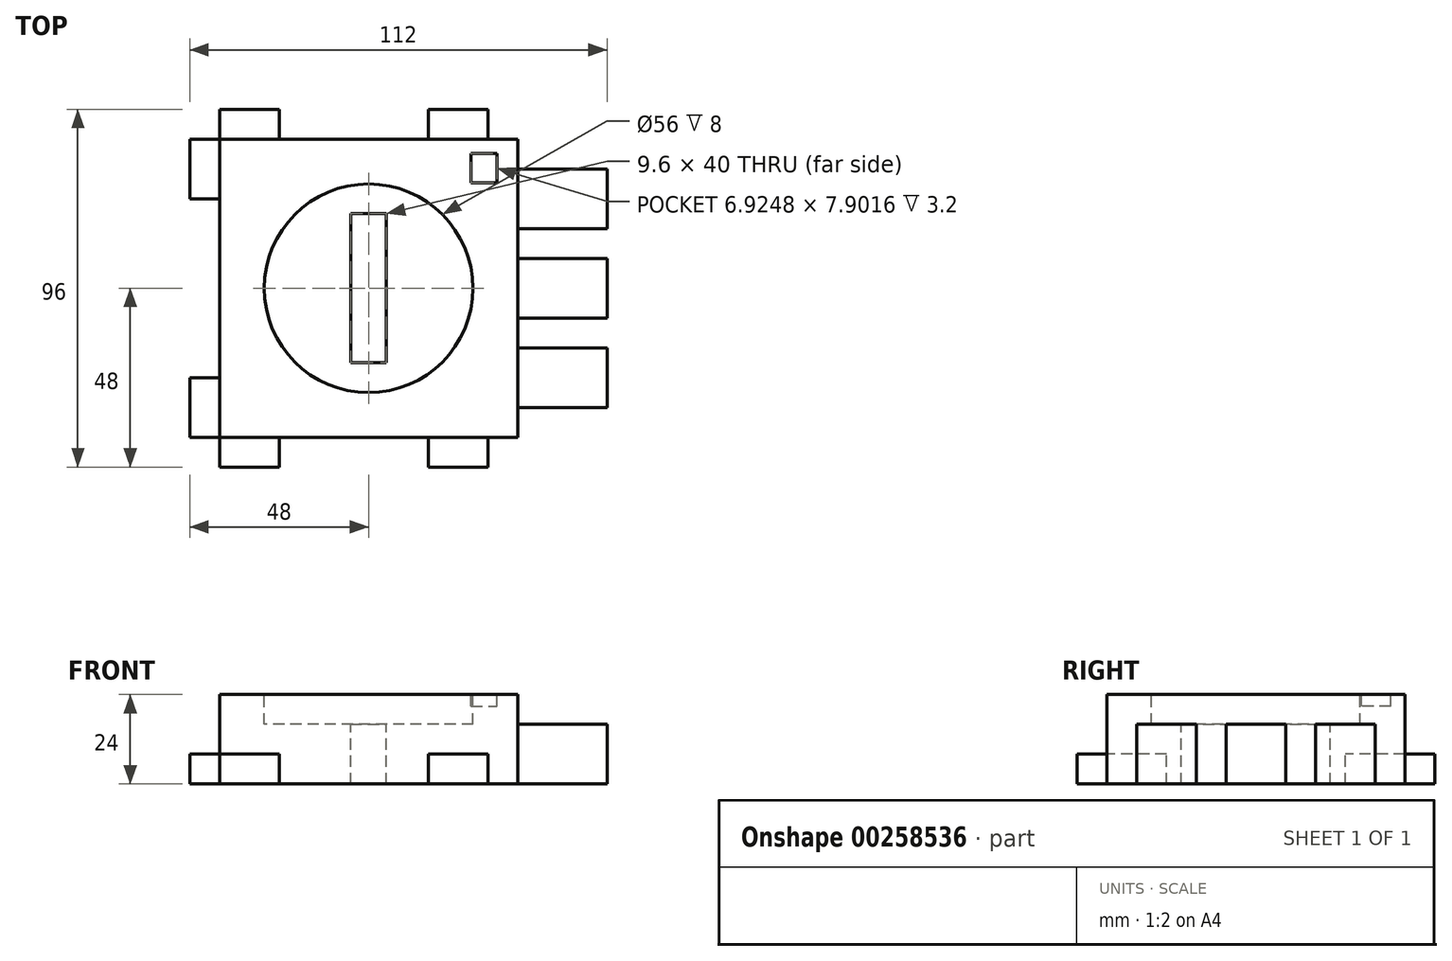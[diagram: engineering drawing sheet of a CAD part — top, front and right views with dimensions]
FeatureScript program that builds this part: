
annotation { "Feature Type Name" : "Feature", "Feature Type Description" : "" }
export const myFeature = defineFeature(function(context is Context, id is Id, definition is map)
    precondition{}
    {
        {
            var Q0;
            Q0=qCreatedBy(makeId("Top.planeOp"),FACE);
            var sketch = newSketch(context, id + "F0", { "sketchPlane" : qUnion([Q0])});
            skLineSegment(sketch, "E0.bottom", {"start": v(-25, 25) * mm, "end": v(25, 25) * mm});
            skLineSegment(sketch, "E0.top", {"start": v(-25, -25) * mm, "end": v(25, -25) * mm});
            skLineSegment(sketch, "E0.left", {"start": v(-25, 25) * mm, "end": v(-25, -25) * mm});
            skLineSegment(sketch, "E0.right", {"start": v(25, 25) * mm, "end": v(25, -25) * mm});
            skPoint(sketch, "E0.middle", {"position": v(0, 0) * mm});
            skLineSegment(sketch, "E1.0", {"start": v(-30, 30) * mm, "end": v(25, 30) * mm});
            skLineSegment(sketch, "E1.1", {"start": v(-30, 30) * mm, "end": v(-30, -30) * mm});
            skLineSegment(sketch, "E1.2", {"start": v(-30, -30) * mm, "end": v(25, -30) * mm});
            skLineSegment(sketch, "E2", {"start": v(25, 30) * mm, "end": v(25, 25) * mm});
            skLineSegment(sketch, "E3", {"start": v(25, -25) * mm, "end": v(25, -30) * mm});
            skSolve(sketch);
        }
        {
            var Q0;
            Q0=makeQuery(id+"F0.imprint","IMPRINT",FACE,{"disambiguationData":[TD([[makeQuery(id+"F0.imprint","IMPRINT",EDGE,{"derivedFrom":sQuery(id+"F0.wireOp",EDGE,"E0.bottom")}),-1.0]])]});
            extrude(context, id + "F1", {"entities" : qUnion([Q0]), "depth" : 15 * mm});
        }
        {
            var Q0;
            Q0=makeQuery(id+"F1.opExtrude","CAP_FACE",FACE,{"disambiguationData":[OSD([sQuery(id+"F0.wireOp",EDGE,"E0.bottom"),sQuery(id+"F0.wireOp",EDGE,"E0.top"),sQuery(id+"F0.wireOp",EDGE,"E0.left"),sQuery(id+"F0.wireOp",EDGE,"E0.right")])],"isStart":false});
            var sketch = newSketch(context, id + "F2", { "sketchPlane" : qUnion([Q0])});
            skLineSegment(sketch, "E4.bottom", {"start": v(-3, 12.5) * mm, "end": v(3, 12.5) * mm});
            skLineSegment(sketch, "E4.top", {"start": v(-3, -12.5) * mm, "end": v(3, -12.5) * mm});
            skLineSegment(sketch, "E4.left", {"start": v(-3, 12.5) * mm, "end": v(-3, -12.5) * mm});
            skLineSegment(sketch, "E4.right", {"start": v(3, 12.5) * mm, "end": v(3, -12.5) * mm});
            skPoint(sketch, "E4.middle", {"position": v(0, 0) * mm});
            skSolve(sketch);
        }
        {
            var Q0;
            Q0=makeQuery(id+"F2.imprint","IMPRINT",FACE,{"disambiguationData":[TD([[makeQuery(id+"F2.imprint","IMPRINT",EDGE,{"derivedFrom":sQuery(id+"F2.wireOp",EDGE,"E4.bottom")}),-1.0]])]});
            extrude(context, id + "F3", {"entities" : qUnion([Q0]), "operationType" : NewBodyOperationType.REMOVE, "oppositeDirection" : true, "depth" : 25 * mm});
        }
        {
            var Q0;
            Q0=makeQuery(id+"F1.opExtrude","SWEPT_FACE",FACE,{"disambiguationData":[OSD([sQuery(id+"F0.wireOp",EDGE,"E0.right")])]});
            var sketch = newSketch(context, id + "F4", { "sketchPlane" : qUnion([Q0])});
            skLineSegment(sketch, "E5.bottom", {"start": v(5, 12.5) * mm, "end": v(-5, 12.5) * mm});
            skLineSegment(sketch, "E5.top", {"start": v(5, 2.5) * mm, "end": v(-5, 2.5) * mm});
            skLineSegment(sketch, "E5.left", {"start": v(5, 12.5) * mm, "end": v(5, 2.5) * mm});
            skLineSegment(sketch, "E5.right", {"start": v(-5, 12.5) * mm, "end": v(-5, 2.5) * mm});
            skPoint(sketch, "E5.middle", {"position": v(0, 7.5) * mm});
            skPoint(sketch, "E5.middle.positionSnap0", {"position": v(-25, 7.5) * mm});
            skPoint(sketch, "E5.centerSnap0", {"position": v(-25, 7.5) * mm});
            skLineSegment(sketch, "E6", {"start": v(-25, 7.5) * mm, "end": v(-5, 7.5) * mm, "construction": true});
            skLineSegment(sketch, "E7", {"start": v(5, 7.5) * mm, "end": v(25, 7.5) * mm, "construction": true});
            skLineSegment(sketch, "E8.bottom", {"start": v(-10, 12.5) * mm, "end": v(-20, 12.5) * mm});
            skLineSegment(sketch, "E8.top", {"start": v(-10, 2.5) * mm, "end": v(-20, 2.5) * mm});
            skLineSegment(sketch, "E8.left", {"start": v(-10, 12.5) * mm, "end": v(-10, 2.5) * mm});
            skLineSegment(sketch, "E8.right", {"start": v(-20, 12.5) * mm, "end": v(-20, 2.5) * mm});
            skPoint(sketch, "E8.middle", {"position": v(-15, 7.5) * mm});
            skLineSegment(sketch, "E9.bottom", {"start": v(20, 12.5) * mm, "end": v(10, 12.5) * mm});
            skLineSegment(sketch, "E9.top", {"start": v(20, 2.5) * mm, "end": v(10, 2.5) * mm});
            skLineSegment(sketch, "E9.left", {"start": v(20, 12.5) * mm, "end": v(20, 2.5) * mm});
            skLineSegment(sketch, "E9.right", {"start": v(10, 12.5) * mm, "end": v(10, 2.5) * mm});
            skPoint(sketch, "E9.middle", {"position": v(15, 7.5) * mm});
            skSolve(sketch);
        }
        {
            var Q0;
            Q0 = qSketchRegion(id + "F4", true);
            extrude(context, id + "F5", {"entities" : qUnion([Q0]), "operationType" : NewBodyOperationType.ADD, "depth" : 30 * mm});
        }
        {
            var Q0;
            Q0=makeQuery(id+"F5.opExtrude","CAP_FACE",FACE,{"disambiguationData":[OSD([sQuery(id+"F4.wireOp",EDGE,"E5.bottom"),sQuery(id+"F4.wireOp",EDGE,"E5.top"),sQuery(id+"F4.wireOp",EDGE,"E5.left"),sQuery(id+"F4.wireOp",EDGE,"E5.right")])],"isStart":false});
            var sketch = newSketch(context, id + "F6", { "sketchPlane" : qUnion([Q0])});
            skLineSegment(sketch, "E10.bottom", {"start": v(25, 17.5) * mm, "end": v(-25, 17.5) * mm});
            skLineSegment(sketch, "E10.top", {"start": v(25, -2.5) * mm, "end": v(-25, -2.5) * mm});
            skLineSegment(sketch, "E10.left", {"start": v(25, 17.5) * mm, "end": v(25, -2.5) * mm});
            skLineSegment(sketch, "E10.right", {"start": v(-25, 17.5) * mm, "end": v(-25, -2.5) * mm});
            skPoint(sketch, "E10.middle", {"position": v(0, 7.5) * mm});
            skPoint(sketch, "E10.middle.positionSnap0", {"position": v(-5, 7.5) * mm});
            skPoint(sketch, "E10.centerSnap0", {"position": v(-5, 7.5) * mm});
            skSolve(sketch);
        }
        {
            var Q0;
            Q0 = qSketchRegion(id + "F6", true);
            extrude(context, id + "F7", {"entities" : qUnion([Q0]), "operationType" : NewBodyOperationType.ADD, "depth" : 30 * mm});
        }
        {
            var Q0;
            Q0=makeQuery(id+"F7.opExtrude","SWEPT_FACE",FACE,{"disambiguationData":[OSD([sQuery(id+"F6.wireOp",EDGE,"E10.left")])]});
            var sketch = newSketch(context, id + "F8", { "sketchPlane" : qUnion([Q0])});
            skLineSegment(sketch, "E11", {"start": v(-85, 17.5) * mm, "end": v(-70, 17.5) * mm, "construction": true});
            skLineSegment(sketch, "E12", {"start": v(-70, 17.5) * mm, "end": v(-85, -2.5) * mm});
            skSolve(sketch);
        }
        {
            var Q0;
            Q0 = qSketchRegion(id + "F8", true);
            var Q1;
            {var subQ0=sQuery(id+"F8.wireOp",EDGE,"E12");Q1=makeQuery(id+"F8.imprint","IMPRINT",FACE,{"disambiguationData":[TD([[makeQuery(id+"F8.imprint","IMPRINT",EDGE,{"derivedFrom":subQ0}),-1.0]])]});}
            extrude(context, id + "F9", {"entities" : qUnion([Q0, Q1]), "operationType" : NewBodyOperationType.REMOVE, "oppositeDirection" : true, "depth" : 50 * mm});
        }
        {
            var Q0;
            Q0=makeQuery(id+"F0.imprint","IMPRINT",FACE,{"disambiguationData":[TD([[makeQuery(id+"F0.imprint","IMPRINT",EDGE,{"derivedFrom":sQuery(id+"F0.wireOp",EDGE,"E0.bottom")}),1.0]])]});
            extrude(context, id + "F10", {"entities" : qUnion([Q0]), "operationType" : NewBodyOperationType.ADD, "depth" : 5 * mm});
        }
        {
            var Q0;
            Q0=makeQuery(id+"F1.opExtrude","CAP_FACE",FACE,{"disambiguationData":[OSD([sQuery(id+"F0.wireOp",EDGE,"E0.bottom"),sQuery(id+"F0.wireOp",EDGE,"E0.top"),sQuery(id+"F0.wireOp",EDGE,"E0.left"),sQuery(id+"F0.wireOp",EDGE,"E0.right")])],"isStart":false});
            var sketch = newSketch(context, id + "F11", { "sketchPlane" : qUnion([Q0])});
            skCircle(sketch, "E13", {"center": v(0, 0) * mm, "radius": 17.5 * mm});
            skLineSegment(sketch, "E14.bottom", {"start": v(-25, 25) * mm, "end": v(-30, 25) * mm});
            skLineSegment(sketch, "E14.top", {"start": v(-25, 30) * mm, "end": v(-30, 30) * mm});
            skLineSegment(sketch, "E14.left", {"start": v(-25, 25) * mm, "end": v(-25, 30) * mm});
            skLineSegment(sketch, "E14.right", {"start": v(-30, 25) * mm, "end": v(-30, 30) * mm});
            skLineSegment(sketch, "E15.bottom", {"start": v(-25, -25) * mm, "end": v(-30, -25) * mm});
            skLineSegment(sketch, "E15.top", {"start": v(-25, -30.14) * mm, "end": v(-30, -30.14) * mm});
            skLineSegment(sketch, "E15.left", {"start": v(-25, -25) * mm, "end": v(-25, -30.14) * mm});
            skLineSegment(sketch, "E15.right", {"start": v(-30, -25) * mm, "end": v(-30, -30.14) * mm});
            skLineSegment(sketch, "E16.bottom", {"start": v(25, 25) * mm, "end": v(20, 25) * mm});
            skLineSegment(sketch, "E16.top", {"start": v(25, 30) * mm, "end": v(20, 30) * mm});
            skLineSegment(sketch, "E16.left", {"start": v(25, 25) * mm, "end": v(25, 30) * mm});
            skLineSegment(sketch, "E16.right", {"start": v(20, 25) * mm, "end": v(20, 30) * mm});
            skLineSegment(sketch, "E17.bottom", {"start": v(25, -25) * mm, "end": v(20, -25) * mm});
            skLineSegment(sketch, "E17.top", {"start": v(25, -30.14) * mm, "end": v(20, -30.14) * mm});
            skLineSegment(sketch, "E17.left", {"start": v(25, -25) * mm, "end": v(25, -30.14) * mm});
            skLineSegment(sketch, "E17.right", {"start": v(20, -25) * mm, "end": v(20, -30.14) * mm});
            skLineSegment(sketch, "E18", {"start": v(20, 30) * mm, "end": v(10, 30) * mm, "construction": true});
            skLineSegment(sketch, "E19", {"start": v(-25, 30) * mm, "end": v(-15, 30) * mm, "construction": true});
            skLineSegment(sketch, "E20.bottom", {"start": v(-15, 30) * mm, "end": v(10, 30) * mm});
            skLineSegment(sketch, "E20.top", {"start": v(-15, 25) * mm, "end": v(10, 25) * mm});
            skLineSegment(sketch, "E20.left", {"start": v(-15, 30) * mm, "end": v(-15, 25) * mm});
            skLineSegment(sketch, "E20.right", {"start": v(10, 30) * mm, "end": v(10, 25) * mm});
            skLineSegment(sketch, "E21.bottom", {"start": v(10, -25) * mm, "end": v(-15, -25) * mm});
            skLineSegment(sketch, "E21.top", {"start": v(10, -30.14) * mm, "end": v(-15, -30.14) * mm});
            skLineSegment(sketch, "E21.left", {"start": v(10, -25) * mm, "end": v(10, -30.14) * mm});
            skLineSegment(sketch, "E21.right", {"start": v(-15, -25) * mm, "end": v(-15, -30.14) * mm});
            skLineSegment(sketch, "E22", {"start": v(-25, 25) * mm, "end": v(-25, 15) * mm, "construction": true});
            skLineSegment(sketch, "E23", {"start": v(-25, -25) * mm, "end": v(-25, -15) * mm, "construction": true});
            skLineSegment(sketch, "E24.bottom", {"start": v(-25, -15) * mm, "end": v(-30, -15) * mm});
            skLineSegment(sketch, "E24.top", {"start": v(-25, 15) * mm, "end": v(-30, 15) * mm});
            skLineSegment(sketch, "E24.left", {"start": v(-25, -15) * mm, "end": v(-25, 15) * mm});
            skLineSegment(sketch, "E24.right", {"start": v(-30, -15) * mm, "end": v(-30, 15) * mm});
            skLineSegment(sketch, "E25.bottom", {"start": v(17.2, 22.6) * mm, "end": v(21.54, 22.6) * mm});
            skLineSegment(sketch, "E25.top", {"start": v(17.2, 17.67) * mm, "end": v(21.54, 17.67) * mm});
            skLineSegment(sketch, "E25.left", {"start": v(17.2, 22.6) * mm, "end": v(17.2, 17.67) * mm});
            skLineSegment(sketch, "E25.right", {"start": v(21.54, 22.6) * mm, "end": v(21.54, 17.67) * mm});
            skSolve(sketch);
        }
        {
            var Q0;
            Q0=makeQuery(id+"F11.imprint","IMPRINT",FACE,{"disambiguationData":[TD([[makeQuery(id+"F11.imprint","IMPRINT",EDGE,{"derivedFrom":sQuery(id+"F11.wireOp",EDGE,"E13")}),1.0]])]});
            extrude(context, id + "F12", {"entities" : qUnion([Q0]), "operationType" : NewBodyOperationType.REMOVE, "oppositeDirection" : true, "depth" : 5 * mm});
        }
        {
            var Q0;
            Q0=makeQuery(id+"F11.imprint","IMPRINT",FACE,{"disambiguationData":[TD([[makeQuery(id+"F11.imprint","IMPRINT",EDGE,{"derivedFrom":sQuery(id+"F11.wireOp",EDGE,"E21.bottom")}),-1.0]])]});
            var Q1;
            Q1=makeQuery(id+"F11.imprint","IMPRINT",FACE,{"disambiguationData":[TD([[makeQuery(id+"F11.imprint","IMPRINT",EDGE,{"derivedFrom":sQuery(id+"F11.wireOp",EDGE,"E15.bottom")}),1.0]])]});
            var Q2;
            Q2=makeQuery(id+"F11.imprint","IMPRINT",FACE,{"disambiguationData":[TD([[makeQuery(id+"F11.imprint","IMPRINT",EDGE,{"derivedFrom":sQuery(id+"F11.wireOp",EDGE,"E17.bottom")}),-1.0]])]});
            var Q3;
            Q3=makeQuery(id+"F11.imprint","IMPRINT",FACE,{"disambiguationData":[TD([[makeQuery(id+"F11.imprint","IMPRINT",EDGE,{"derivedFrom":sQuery(id+"F11.wireOp",EDGE,"E16.bottom")}),1.0]])]});
            var Q4;
            Q4=makeQuery(id+"F11.imprint","IMPRINT",FACE,{"disambiguationData":[TD([[makeQuery(id+"F11.imprint","IMPRINT",EDGE,{"derivedFrom":sQuery(id+"F11.wireOp",EDGE,"E20.bottom")}),-1.0]])]});
            var Q5;
            Q5=makeQuery(id+"F11.imprint","IMPRINT",FACE,{"disambiguationData":[TD([[makeQuery(id+"F11.imprint","IMPRINT",EDGE,{"derivedFrom":sQuery(id+"F11.wireOp",EDGE,"E14.bottom")}),-1.0]])]});
            var Q6;
            Q6=makeQuery(id+"F11.imprint","IMPRINT",FACE,{"disambiguationData":[TD([[makeQuery(id+"F11.imprint","IMPRINT",EDGE,{"derivedFrom":sQuery(id+"F11.wireOp",EDGE,"E24.bottom")}),-1.0]])]});
            extrude(context, id + "F13", {"entities" : qUnion([Q0, Q1, Q2, Q3, Q4, Q5, Q6]), "operationType" : NewBodyOperationType.REMOVE, "oppositeDirection" : true, "depth" : 25 * mm});
        }
        {
            var Q0;
            Q0=makeQuery(id+"F7.opExtrude","SWEPT_FACE",FACE,{"disambiguationData":[OSD([sQuery(id+"F6.wireOp",EDGE,"E10.bottom")])]});
            var sketch = newSketch(context, id + "F14", { "sketchPlane" : qUnion([Q0])});
            skLineSegment(sketch, "E26.bottom", {"start": v(70, -25) * mm, "end": v(64, -25) * mm});
            skLineSegment(sketch, "E26.top", {"start": v(70, -31) * mm, "end": v(64, -31) * mm});
            skLineSegment(sketch, "E26.left", {"start": v(70, -25) * mm, "end": v(70, -31) * mm});
            skLineSegment(sketch, "E26.right", {"start": v(64, -25) * mm, "end": v(64, -31) * mm});
            skLineSegment(sketch, "E27.bottom", {"start": v(70, 25) * mm, "end": v(64, 25) * mm});
            skLineSegment(sketch, "E27.top", {"start": v(70, 31) * mm, "end": v(64, 31) * mm});
            skLineSegment(sketch, "E27.left", {"start": v(70, 25) * mm, "end": v(70, 31) * mm});
            skLineSegment(sketch, "E27.right", {"start": v(64, 25) * mm, "end": v(64, 31) * mm});
            skSolve(sketch);
        }
        {
            var Q0;
            Q0=makeQuery(id+"F14.imprint","IMPRINT",FACE,{"disambiguationData":[TD([[makeQuery(id+"F14.imprint","IMPRINT",EDGE,{"derivedFrom":sQuery(id+"F14.wireOp",EDGE,"E27.bottom")}),-1.0]])]});
            var Q1;
            Q1=makeQuery(id+"F14.imprint","IMPRINT",FACE,{"disambiguationData":[TD([[makeQuery(id+"F14.imprint","IMPRINT",EDGE,{"derivedFrom":sQuery(id+"F14.wireOp",EDGE,"E26.bottom")}),1.0]])]});
            extrude(context, id + "F15", {"entities" : qUnion([Q0, Q1]), "operationType" : NewBodyOperationType.ADD, "oppositeDirection" : true, "depth" : 20 * mm});
        }
        {
            var Q0;
            Q0=makeQuery(id+"F14.imprint","IMPRINT",FACE,{"disambiguationData":[TD([[makeQuery(id+"F14.imprint","IMPRINT",EDGE,{"derivedFrom":sQuery(id+"F14.wireOp",EDGE,"E26.bottom")}),1.0]])]});
            var Q1;
            Q1=makeQuery(id+"F14.imprint","IMPRINT",FACE,{"disambiguationData":[TD([[makeQuery(id+"F14.imprint","IMPRINT",EDGE,{"derivedFrom":sQuery(id+"F14.wireOp",EDGE,"E27.bottom")}),-1.0]])]});
            extrude(context, id + "F16", {"entities" : qUnion([Q0, Q1]), "operationType" : NewBodyOperationType.REMOVE, "oppositeDirection" : true, "depth" : 15 * mm});
        }
        {
            var Q0;
            Q0=makeQuery(id+"F11.imprint","IMPRINT",FACE,{"disambiguationData":[TD([[makeQuery(id+"F11.imprint","IMPRINT",EDGE,{"derivedFrom":sQuery(id+"F11.wireOp",EDGE,"E25.bottom")}),-1.0]])]});
            extrude(context, id + "F17", {"entities" : qUnion([Q0]), "operationType" : NewBodyOperationType.REMOVE, "oppositeDirection" : true, "depth" : 2 * mm});
        }
        {
            var Q0;
            Q0=makeQuery(id+"F15.boolean.opBoolean","MERGE",FACE,{"derivedFrom":[makeQuery(id+"F7.opExtrude","SWEPT_FACE",FACE,{"disambiguationData":[OSD([sQuery(id+"F6.wireOp",EDGE,"E10.bottom")])]}),makeQuery(id+"F15.opExtrude","CAP_FACE",FACE,{"disambiguationData":[OSD([sQuery(id+"F14.wireOp",EDGE,"E26.bottom"),sQuery(id+"F14.wireOp",EDGE,"E26.top"),sQuery(id+"F14.wireOp",EDGE,"E26.left"),sQuery(id+"F14.wireOp",EDGE,"E26.right")])],"isStart":true}),makeQuery(id+"F15.opExtrude","CAP_FACE",FACE,{"disambiguationData":[OSD([sQuery(id+"F14.wireOp",EDGE,"E27.bottom"),sQuery(id+"F14.wireOp",EDGE,"E27.top"),sQuery(id+"F14.wireOp",EDGE,"E27.left"),sQuery(id+"F14.wireOp",EDGE,"E27.right")])],"isStart":true})]});
            var sketch = newSketch(context, id + "F18", { "sketchPlane" : qUnion([Q0])});
            skLineSegment(sketch, "E28.bottom", {"start": v(40, 31) * mm, "end": v(100, 31) * mm});
            skLineSegment(sketch, "E28.top", {"start": v(40, -31) * mm, "end": v(100, -31) * mm});
            skLineSegment(sketch, "E28.left", {"start": v(40, 31) * mm, "end": v(40, -31) * mm});
            skLineSegment(sketch, "E28.right", {"start": v(100, 31) * mm, "end": v(100, -31) * mm});
            skPoint(sketch, "E28.middle", {"position": v(70, 0) * mm});
            skSolve(sketch);
        }
        {
            var Q0;
            Q0 = qSketchRegion(id + "F18", true);
            extrude(context, id + "F19", {"entities" : qUnion([Q0]), "operationType" : NewBodyOperationType.REMOVE, "oppositeDirection" : true, "depth" : 25 * mm});
        }
        {
            var Q0;
            Q0=makeQuery(id+"F1.opExtrude","SWEPT_BODY",BODY,{"disambiguationData":[OSD([sQuery(id+"F0.wireOp",EDGE,"E0.bottom"),sQuery(id+"F0.wireOp",EDGE,"E0.top"),sQuery(id+"F0.wireOp",EDGE,"E0.left"),sQuery(id+"F0.wireOp",EDGE,"E0.right")])]});
            var Q1;
            Q1=sQuery(id+"F11.wireOp",VERTEX,"E13.center");
            transform(context, id + "F20", {"entities" : qUnion([Q0]), "transformType" : TransformType.SCALE_UNIFORMLY, "scale" : 1.6, "scalePoint" : qUnion([Q1]), "makeCopy" : false});
        }
        {
            var Q0;
            Q0=makeQuery(id+"F5.opExtrude","SWEPT_FACE",FACE,{"disambiguationData":[OSD([sQuery(id+"F4.wireOp",EDGE,"E9.top")])]});
            var Q1;
            Q1=makeQuery(id+"F5.opExtrude","SWEPT_FACE",FACE,{"disambiguationData":[OSD([sQuery(id+"F4.wireOp",EDGE,"E5.top")])]});
            var Q2;
            Q2=makeQuery(id+"F5.opExtrude","SWEPT_FACE",FACE,{"disambiguationData":[OSD([sQuery(id+"F4.wireOp",EDGE,"E8.top")])]});
            extrude(context, id + "F21", {"entities" : qUnion([Q0, Q1, Q2]), "operationType" : NewBodyOperationType.ADD, "depth" : 4 * mm});
        }
        {
            var Q0;
            Q0=makeQuery(id+"F5.opExtrude","SWEPT_FACE",FACE,{"disambiguationData":[OSD([sQuery(id+"F4.wireOp",EDGE,"E9.bottom")])]});
            var Q1;
            Q1=makeQuery(id+"F5.opExtrude","SWEPT_FACE",FACE,{"disambiguationData":[OSD([sQuery(id+"F4.wireOp",EDGE,"E5.bottom")])]});
            var Q2;
            Q2=makeQuery(id+"F5.opExtrude","SWEPT_FACE",FACE,{"disambiguationData":[OSD([sQuery(id+"F4.wireOp",EDGE,"E8.bottom")])]});
            extrude(context, id + "F22", {"entities" : qUnion([Q0, Q1, Q2]), "operationType" : NewBodyOperationType.REMOVE, "oppositeDirection" : true, "depth" : 4 * mm});
        }
    });
